FCSTD DOCUMENT  (FreeCAD 0.16R6706 (Git))
Label: Ejercicio 4
License: All rights reserved
LicenseURL: http://en.wikipedia.org/wiki/All_rights_reserved
objects: Sketcher::SketchObject×1
note: 1 computed .brp shape members not serialized (recipe doc carries the construction recipe); baked Part::Feature solids carry a one-line shape summary decoded from their .brp

FEATURE [Sketcher::SketchObject] Sketch
  sketch-geometry (29):
    g0: LineSegment StartX=-89.5962 StartY=-32.6802 StartZ=0 EndX=90.2941 EndY=-32.6802 EndZ=0
    g1: LineSegment StartX=90.2941 StartY=-32.6802 StartZ=0 EndX=90.2941 EndY=28.0938 EndZ=0
    g2: LineSegment StartX=90.2941 StartY=28.0938 StartZ=0 EndX=-89.5962 EndY=28.0938 EndZ=0
    g3: LineSegment StartX=-89.5962 StartY=28.0938 StartZ=0 EndX=-89.5962 EndY=-32.6802 EndZ=0
    g4: Ellipse CenterX=-110.094 CenterY=2.98783 CenterZ=0 NormalX=0 NormalY=0 NormalZ=1 MajorRadius=50.1867 MinorRadius=30.0847 AngleXU=-0.00704214
    g5: LineSegment [constr] StartX=-59.909 StartY=2.63441 StartZ=0 EndX=-160.28 EndY=3.34125 EndZ=0
    g6: LineSegment [constr] StartX=-109.883 StartY=33.0718 StartZ=0 EndX=-110.306 EndY=-27.0961 EndZ=0
    g7: GeomPoint [constr] X=-69.9256 Y=2.70495 Z=0
    g8: GeomPoint [constr] X=-150.263 Y=3.27071 Z=0
    g9: Ellipse CenterX=110.439 CenterY=2.98783 CenterZ=0 NormalX=0 NormalY=0 NormalZ=1 MajorRadius=50.1855 MinorRadius=30.7475 AngleXU=-3.14159
    g10: LineSegment [constr] StartX=60.2535 StartY=2.98783 StartZ=0 EndX=160.624 EndY=2.98783 EndZ=0
    g11: LineSegment [constr] StartX=110.439 StartY=-27.7596 StartZ=0 EndX=110.439 EndY=33.7353 EndZ=0
    g12: GeomPoint [constr] X=70.7757 Y=2.98783 Z=0
    g13: GeomPoint [constr] X=150.102 Y=2.98783 Z=0
    g14: Ellipse CenterX=52.1078 CenterY=-31.9899 CenterZ=0 NormalX=0 NormalY=0 NormalZ=1 MajorRadius=52.1336 MinorRadius=24.9083 AngleXU=-0.00908844
    g15: LineSegment [constr] StartX=104.239 StartY=-32.4637 StartZ=0 EndX=-0.0236593 EndY=-31.5161 EndZ=0
    g16: LineSegment [constr] StartX=52.3342 StartY=-7.08258 StartZ=0 EndX=51.8815 EndY=-56.8972 EndZ=0
    g17: GeomPoint [constr] X=97.9043 Y=-32.4061 Z=0
    g18: GeomPoint [constr] X=6.31134 Y=-31.5737 Z=0
    g19: Ellipse CenterX=-52.1156 CenterY=-32.6802 CenterZ=0 NormalX=0 NormalY=0 NormalZ=1 MajorRadius=52.1208 MinorRadius=25.3327 AngleXU=0.00864303
    g20: LineSegment [constr] StartX=0.00320752 StartY=-32.2297 StartZ=0 EndX=-104.234 EndY=-33.1307 EndZ=0
    g21: LineSegment [constr] StartX=-52.3346 StartY=-7.34845 StartZ=0 EndX=-51.8967 EndY=-58.012 EndZ=0
    g22: GeomPoint [constr] X=-6.56702 Y=-32.2865 Z=0
    g23: GeomPoint [constr] X=-97.6642 Y=-33.0739 Z=0
    g24: Ellipse CenterX=0.143711 CenterY=28.0938 CenterZ=0 NormalX=0 NormalY=0 NormalZ=1 MajorRadius=25.3499 MinorRadius=11.103 AngleXU=-0.00944935
    g25: LineSegment [constr] StartX=25.4925 StartY=27.8543 StartZ=0 EndX=-25.2051 EndY=28.3333 EndZ=0
    g26: LineSegment [constr] StartX=0.248625 StartY=39.1963 StartZ=0 EndX=0.038796 EndY=16.9913 EndZ=0
    g27: GeomPoint [constr] X=22.9317 Y=27.8785 Z=0
    g28: GeomPoint [constr] X=-22.6443 Y=28.3091 Z=0
  constraints (16):
    c: Coincident(g0,g1)
    c: Coincident(g1,g2)
    c: Coincident(g2,g3)
    c: Coincident(g3,g0)
    c: Horizontal(g0)
    c: Horizontal(g2)
    c: Vertical(g1)
    c: Vertical(g3)
    c: InternalAlignment(g5-g8 -> g4) x4
    c: InternalAlignment(g10-g13 -> g9) x4
    c: InternalAlignment(g15-g18 -> g14) x4
    c: InternalAlignment(g20-g23 -> g19) x4
    c: PointOnObject(g19,g0)
    c: PointOnObject(g15,g19)
    c: InternalAlignment(g25-g28 -> g24) x4
    c: PointOnObject(g24,g2)
